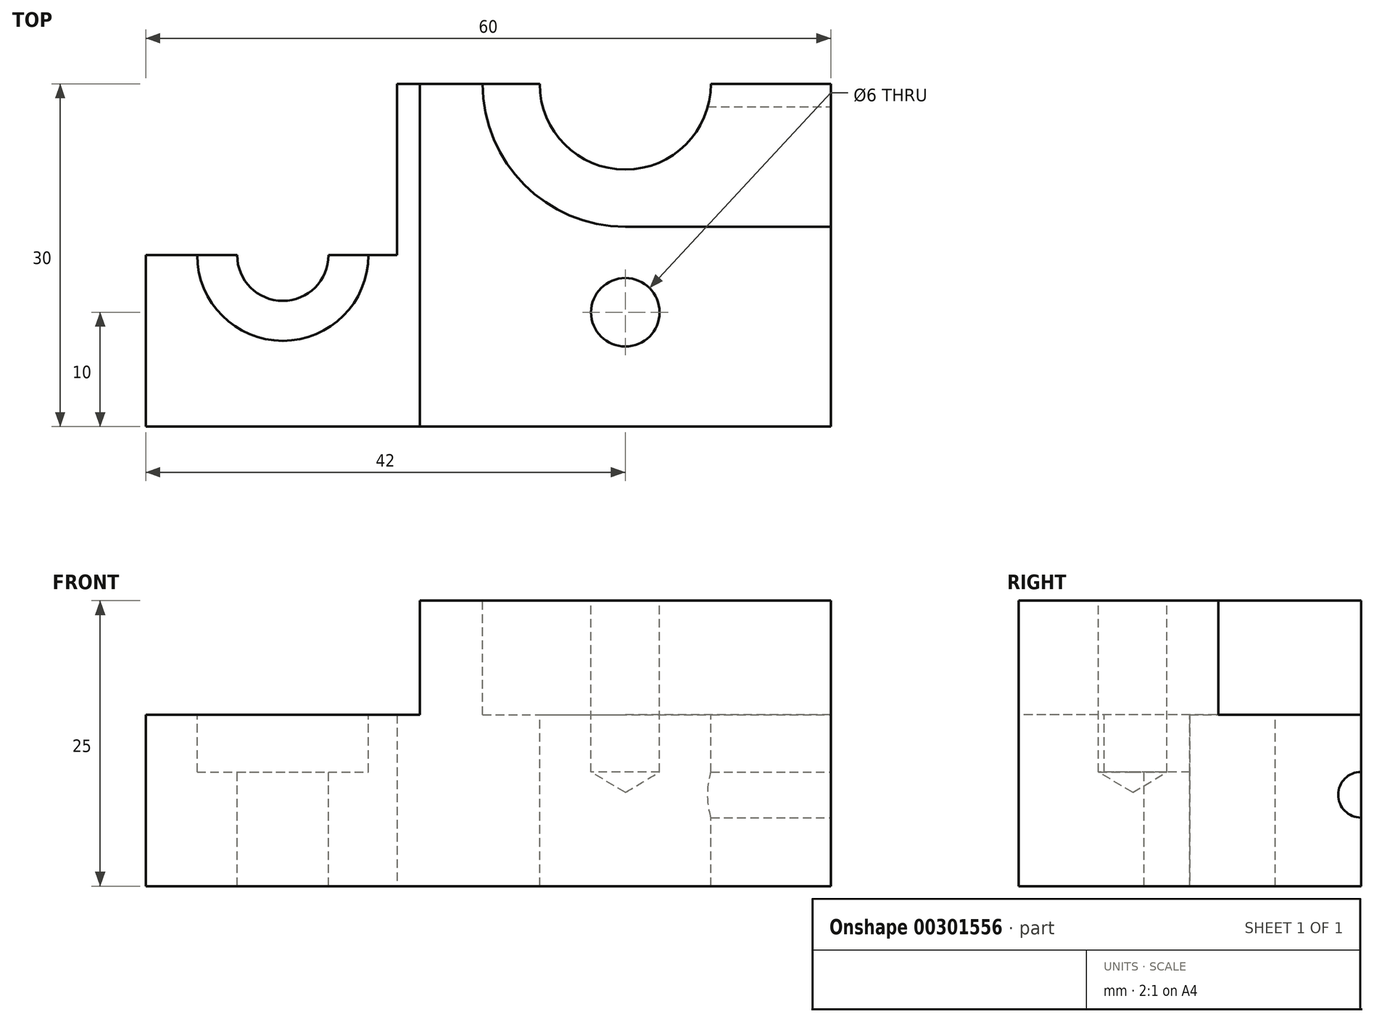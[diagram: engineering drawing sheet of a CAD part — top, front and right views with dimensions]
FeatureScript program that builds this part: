
annotation { "Feature Type Name" : "Feature", "Feature Type Description" : "" }
export const myFeature = defineFeature(function(context is Context, id is Id, definition is map)
    precondition{}
    {
        {
            var Q0;
            Q0=qCreatedBy(makeId("Top.planeOp"),FACE);
            var sketch = newSketch(context, id + "F0", { "sketchPlane" : qUnion([Q0])});
            skLineSegment(sketch, "E0.bottom", {"start": v(-30, 30) * mm, "end": v(30, 30) * mm});
            skLineSegment(sketch, "E0.top", {"start": v(-30, -30) * mm, "end": v(30, -30) * mm});
            skLineSegment(sketch, "E0.left", {"start": v(-30, 30) * mm, "end": v(-30, -30) * mm});
            skLineSegment(sketch, "E0.right", {"start": v(30, 30) * mm, "end": v(30, -30) * mm});
            skPoint(sketch, "E0.middle", {"position": v(0, 0) * mm});
            skSolve(sketch);
        }
        {
            var Q0;
            Q0=makeQuery(id+"F0.imprint","IMPRINT",FACE,{"disambiguationData":[TD([[makeQuery(id+"F0.imprint","IMPRINT",EDGE,{"derivedFrom":sQuery(id+"F0.wireOp",EDGE,"E0.bottom")}),-1.0]])]});
            extrude(context, id + "F1", {"entities" : qUnion([Q0]), "depth" : 25 * mm});
        }
        {
            var Q0;
            Q0=makeQuery(id+"F1.opExtrude","CAP_FACE",FACE,{"disambiguationData":[OSD([sQuery(id+"F0.wireOp",EDGE,"E0.bottom"),sQuery(id+"F0.wireOp",EDGE,"E0.top"),sQuery(id+"F0.wireOp",EDGE,"E0.left"),sQuery(id+"F0.wireOp",EDGE,"E0.right")])],"isStart":false});
            var sketch = newSketch(context, id + "F2", { "sketchPlane" : qUnion([Q0])});
            skLineSegment(sketch, "E1.bottom", {"start": v(-30, 30) * mm, "end": v(-6, 30) * mm});
            skLineSegment(sketch, "E1.top", {"start": v(-30, -30) * mm, "end": v(-6, -30) * mm});
            skLineSegment(sketch, "E1.left", {"start": v(-30, 30) * mm, "end": v(-30, -30) * mm});
            skLineSegment(sketch, "E1.right", {"start": v(-6, 30) * mm, "end": v(-6, -30) * mm});
            skLineSegment(sketch, "E2.bottom", {"start": v(30, 12.5) * mm, "end": v(12, 12.5) * mm});
            skLineSegment(sketch, "E2.top", {"start": v(30, -12.5) * mm, "end": v(12, -12.5) * mm});
            skLineSegment(sketch, "E2.left", {"start": v(30, 12.5) * mm, "end": v(30, -12.5) * mm});
            skPoint(sketch, "E2.middle", {"position": v(21, 0) * mm});
            skArc(sketch, "E3", {"start": v(12, 12.5) * mm, "mid": v(-0.5, 0) * mm, "end": v(12, -12.5) * mm});
            skSolve(sketch);
        }
        {
            var Q0;
            Q0=makeQuery(id+"F2.imprint","IMPRINT",FACE,{"disambiguationData":[TD([[makeQuery(id+"F2.imprint","IMPRINT",EDGE,{"derivedFrom":sQuery(id+"F2.wireOp",EDGE,"E1.bottom")}),-1.0]])]});
            var Q1;
            Q1=makeQuery(id+"F2.imprint","IMPRINT",FACE,{"disambiguationData":[TD([[makeQuery(id+"F2.imprint","IMPRINT",EDGE,{"derivedFrom":sQuery(id+"F2.wireOp",EDGE,"E2.bottom")}),1.0]])]});
            extrude(context, id + "F3", {"entities" : qUnion([Q0, Q1]), "operationType" : NewBodyOperationType.REMOVE, "oppositeDirection" : true, "depth" : 10 * mm});
        }
        {
            var Q0;
            Q0=makeQuery(id+"F3.boolean.opBoolean","COPY",FACE,{"derivedFrom":makeQuery(id+"F3.opExtrude","CAP_FACE",FACE,{"disambiguationData":[OSD([sQuery(id+"F2.wireOp",EDGE,"E1.bottom"),sQuery(id+"F2.wireOp",EDGE,"E1.top"),sQuery(id+"F2.wireOp",EDGE,"E1.left"),sQuery(id+"F2.wireOp",EDGE,"E1.right")])],"isStart":false})});
            var sketch = newSketch(context, id + "F4", { "sketchPlane" : qUnion([Q0])});
            skPoint(sketch, "E4", {"position": v(-18, 15) * mm});
            skPoint(sketch, "E5", {"position": v(-18, -15) * mm});
            skSolve(sketch);
        }
        {
            var Q0;
            Q0=sQuery(id+"F4.wireOp",VERTEX,"E4");
            var Q1;
            Q1=sQuery(id+"F4.wireOp",VERTEX,"E5");
            var Q2;
            Q2=makeQuery(id+"F1.opExtrude","SWEPT_BODY",BODY,{"disambiguationData":[OSD([sQuery(id+"F0.wireOp",EDGE,"E0.bottom"),sQuery(id+"F0.wireOp",EDGE,"E0.top"),sQuery(id+"F0.wireOp",EDGE,"E0.left"),sQuery(id+"F0.wireOp",EDGE,"E0.right")])]});
            hole(context, id + "F5", {"style" : HoleStyle.C_BORE, "endStyle" : HoleEndStyle.THROUGH, "holeDiameter" : 8 * mm, "cBoreDiameter" : 15 * mm, "cBoreDepth" : 5 * mm, "tappedDepth" : 12 * mm, "tapClearance" : 3, "startFromSketch" : true, "locations" : qUnion([Q0, Q1]), "scope" : qUnion([Q2])});
        }
        {
            var Q0;
            Q0=makeQuery(id+"F3.boolean.opBoolean","COPY",FACE,{"derivedFrom":makeQuery(id+"F3.opExtrude","CAP_FACE",FACE,{"disambiguationData":[OSD([sQuery(id+"F2.wireOp",EDGE,"E2.bottom"),sQuery(id+"F2.wireOp",EDGE,"E2.top"),sQuery(id+"F2.wireOp",EDGE,"E2.left"),sQuery(id+"F2.wireOp",EDGE,"E3")])],"isStart":false})});
            var sketch = newSketch(context, id + "F6", { "sketchPlane" : qUnion([Q0])});
            skCircle(sketch, "E6", {"center": v(12, 0) * mm, "radius": 7.5 * mm});
            skSolve(sketch);
        }
        {
            var Q0;
            Q0=makeQuery(id+"F6.imprint","IMPRINT",FACE,{"disambiguationData":[TD([[makeQuery(id+"F6.imprint","IMPRINT",EDGE,{"derivedFrom":sQuery(id+"F6.wireOp",EDGE,"E6")}),1.0]])]});
            extrude(context, id + "F7", {"entities" : qUnion([Q0]), "operationType" : NewBodyOperationType.REMOVE, "endBound" : BoundingType.UP_TO_NEXT, "oppositeDirection" : true, "depth" : 25 * mm});
        }
        {
            var Q0;
            Q0=makeQuery(id+"F1.opExtrude","CAP_FACE",FACE,{"disambiguationData":[OSD([sQuery(id+"F0.wireOp",EDGE,"E0.bottom"),sQuery(id+"F0.wireOp",EDGE,"E0.top"),sQuery(id+"F0.wireOp",EDGE,"E0.left"),sQuery(id+"F0.wireOp",EDGE,"E0.right")])],"isStart":false});
            var sketch = newSketch(context, id + "F8", { "sketchPlane" : qUnion([Q0])});
            skPoint(sketch, "E7", {"position": v(12, 20) * mm});
            skPoint(sketch, "E8", {"position": v(12, -20) * mm});
            skSolve(sketch);
        }
        {
            var Q0;
            Q0=sQuery(id+"F8.wireOp",VERTEX,"E7");
            var Q1;
            Q1=sQuery(id+"F8.wireOp",VERTEX,"E8");
            var Q2;
            Q2=makeQuery(id+"F1.opExtrude","SWEPT_BODY",BODY,{"disambiguationData":[OSD([sQuery(id+"F0.wireOp",EDGE,"E0.bottom"),sQuery(id+"F0.wireOp",EDGE,"E0.top"),sQuery(id+"F0.wireOp",EDGE,"E0.left"),sQuery(id+"F0.wireOp",EDGE,"E0.right")])]});
            hole(context, id + "F9", {"style" : HoleStyle.SIMPLE, "endStyle" : HoleEndStyle.BLIND, "holeDiameter" : 6 * mm, "holeDepth" : 15 * mm, "tappedDepth" : 12 * mm, "tapClearance" : 3, "startFromSketch" : true, "locations" : qUnion([Q0, Q1]), "scope" : qUnion([Q2])});
        }
        {
            var Q0;
            Q0=makeQuery(id+"F1.opExtrude","SWEPT_FACE",FACE,{"disambiguationData":[OSD([sQuery(id+"F0.wireOp",EDGE,"E0.right")])]});
            var sketch = newSketch(context, id + "F10", { "sketchPlane" : qUnion([Q0])});
            skCircle(sketch, "E9", {"center": v(0, 8) * mm, "radius": 2 * mm});
            skSolve(sketch);
        }
        {
            var Q0;
            Q0=makeQuery(id+"F10.imprint","IMPRINT",FACE,{"disambiguationData":[TD([[makeQuery(id+"F10.imprint","IMPRINT",EDGE,{"derivedFrom":sQuery(id+"F10.wireOp",EDGE,"E9")}),1.0]])]});
            extrude(context, id + "F11", {"entities" : qUnion([Q0]), "operationType" : NewBodyOperationType.REMOVE, "endBound" : BoundingType.UP_TO_NEXT, "oppositeDirection" : true, "depth" : 25 * mm});
        }
        {
            var Q0;
            Q0=makeQuery(id+"F3.boolean.opBoolean","COPY",FACE,{"derivedFrom":makeQuery(id+"F3.opExtrude","CAP_FACE",FACE,{"disambiguationData":[OSD([sQuery(id+"F2.wireOp",EDGE,"E1.bottom"),sQuery(id+"F2.wireOp",EDGE,"E1.top"),sQuery(id+"F2.wireOp",EDGE,"E1.left"),sQuery(id+"F2.wireOp",EDGE,"E1.right")])],"isStart":false})});
            var sketch = newSketch(context, id + "F12", { "sketchPlane" : qUnion([Q0])});
            skPoint(sketch, "E10", {"position": v(-18, -15) * mm});
            skSolve(sketch);
        }
        {
            var Q0;
            Q0=qCreatedBy(makeId("Top.planeOp"),FACE);
            var sketch = newSketch(context, id + "F13", { "sketchPlane" : qUnion([Q0])});
            skLineSegment(sketch, "E11", {"start": v(30, 0) * mm, "end": v(30, 30) * mm});
            skLineSegment(sketch, "E12", {"start": v(30, 30) * mm, "end": v(-30, 30) * mm});
            skLineSegment(sketch, "E13", {"start": v(-30, 30) * mm, "end": v(-30, -15) * mm});
            skLineSegment(sketch, "E14", {"start": v(-30, -15) * mm, "end": v(-8, -15) * mm});
            skLineSegment(sketch, "E15", {"start": v(-8, -15) * mm, "end": v(-8, 0) * mm});
            skLineSegment(sketch, "E16", {"start": v(-8, 0) * mm, "end": v(30, 0) * mm});
            skSolve(sketch);
        }
        {
            var Q0;
            Q0=qSketchRegion(id+"F13",true);
            extrude(context, id + "F14", {"entities" : qUnion([Q0]), "operationType" : NewBodyOperationType.REMOVE, "endBound" : BoundingType.UP_TO_NEXT, "depth" : 25 * mm});
        }
    });
